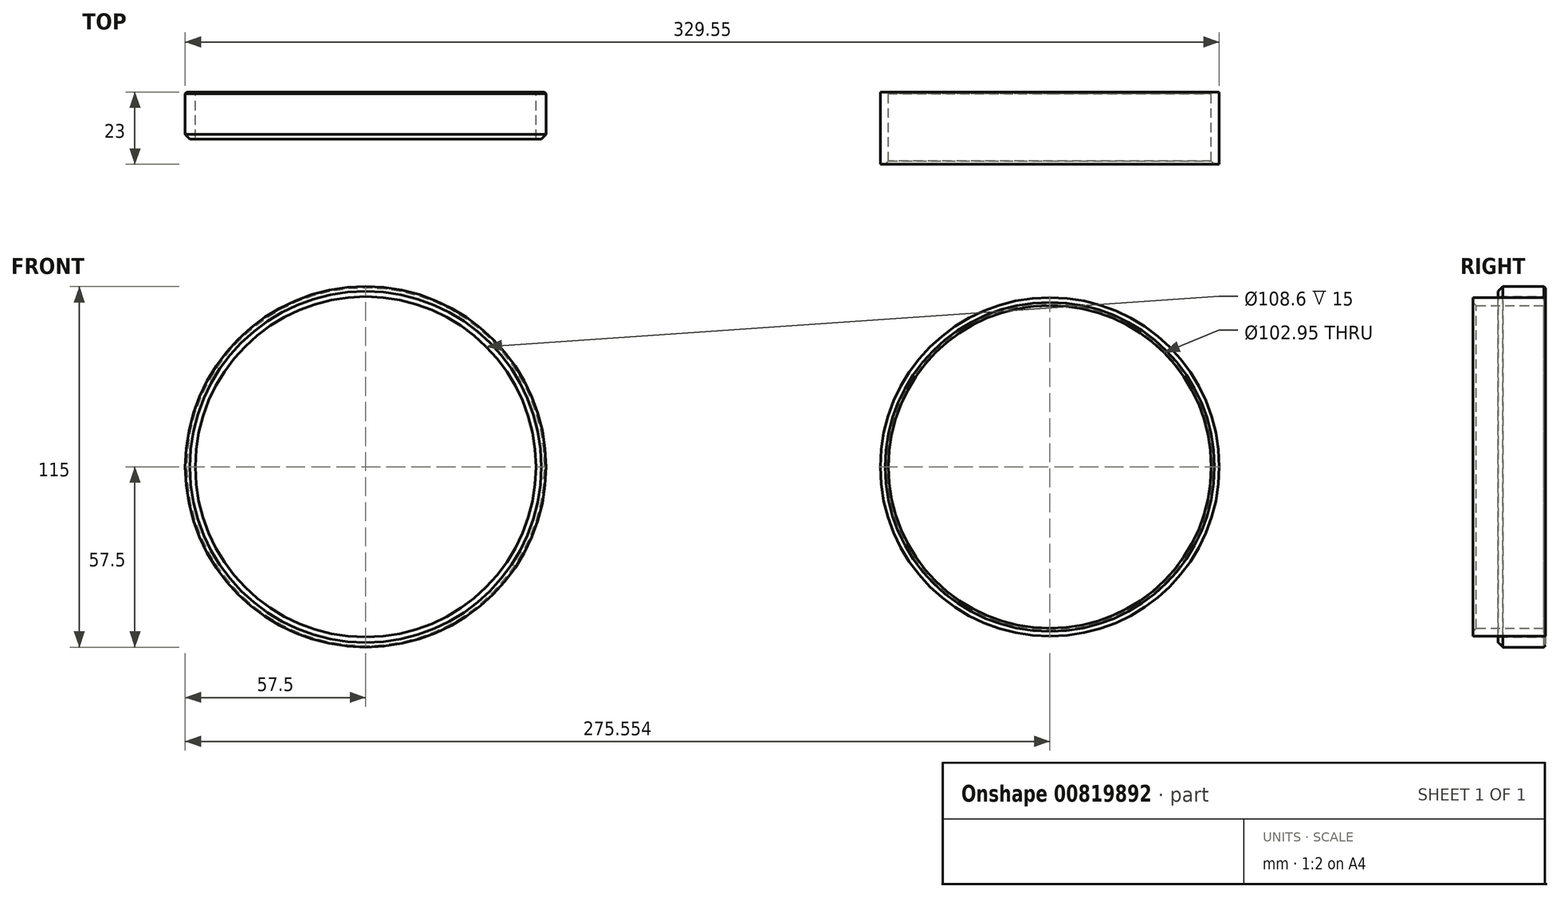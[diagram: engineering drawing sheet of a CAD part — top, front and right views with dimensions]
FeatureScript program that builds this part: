
annotation { "Feature Type Name" : "Feature", "Feature Type Description" : "" }
export const myFeature = defineFeature(function(context is Context, id is Id, definition is map)
    precondition{}
    {
        {
            var Q0;
            Q0=qCreatedBy(makeId("Front.planeOp"),FACE);
            var sketch = newSketch(context, id + "F0", { "sketchPlane" : qUnion([Q0])});
            skCircle(sketch, "E0", {"center": v(0, 0) * mm, "radius": 54.3 * mm});
            skCircle(sketch, "E1", {"center": v(0, 0) * mm, "radius": 57.5 * mm});
            skSolve(sketch);
        }
        {
            var Q0;
            Q0=qCreatedBy(makeId("Front.planeOp"),FACE);
            var sketch = newSketch(context, id + "F1", { "sketchPlane" : qUnion([Q0])});
            skCircle(sketch, "E2", {"center": v(218.05, 0) * mm, "radius": 54 * mm});
            skCircle(sketch, "E3", {"center": v(218.05, 0) * mm, "radius": 51.48 * mm});
            skSolve(sketch);
        }
        {
            var Q0;
            Q0=qSketchRegion(id+"F1",true);
            extrude(context, id + "F2", {"entities" : qUnion([Q0]), "depth" : 23 * mm, "offsetDistance" : 25 * mm});
        }
        {
            var Q0;
            Q0=makeQuery(id+"F2.opExtrude","CAP_EDGE",EDGE,{"disambiguationData":[OSD([sQuery(id+"F1.wireOp",EDGE,"E3")])],"isStart":false});
            chamfer(context, id + "F3", {"entities" : qUnion([Q0]), "width" : 1 * mm, "tangentPropagation" : true});
        }
        {
            var Q0;
            Q0=makeQuery(id+"F2.opExtrude","CAP_EDGE",EDGE,{"disambiguationData":[OSD([sQuery(id+"F1.wireOp",EDGE,"E3")])],"isStart":true});
            chamfer(context, id + "F4", {"entities" : qUnion([Q0]), "width" : .5 * mm, "tangentPropagation" : true});
        }
        {
            var Q0;
            Q0=makeQuery(id+"F0.imprint","IMPRINT",FACE,{"disambiguationData":[TD([[makeQuery(id+"F0.imprint","IMPRINT",EDGE,{"derivedFrom":sQuery(id+"F0.wireOp",EDGE,"E0")}),-1.0]])]});
            extrude(context, id + "F5", {"entities" : qUnion([Q0]), "depth" : 15 * mm, "offsetDistance" : 25 * mm});
        }
        {
            var Q0;
            Q0=makeQuery(id+"F5.opExtrude","CAP_EDGE",EDGE,{"disambiguationData":[OSD([sQuery(id+"F0.wireOp",EDGE,"E1")])],"isStart":false});
            chamfer(context, id + "F6", {"entities" : qUnion([Q0]), "width" : 1.5 * mm, "tangentPropagation" : true});
        }
        {
            var Q0;
            Q0=makeQuery(id+"F5.opExtrude","CAP_EDGE",EDGE,{"disambiguationData":[OSD([sQuery(id+"F0.wireOp",EDGE,"E1")])],"isStart":true});
            chamfer(context, id + "F7", {"entities" : qUnion([Q0]), "width" : .5 * mm, "tangentPropagation" : true});
        }
    });
